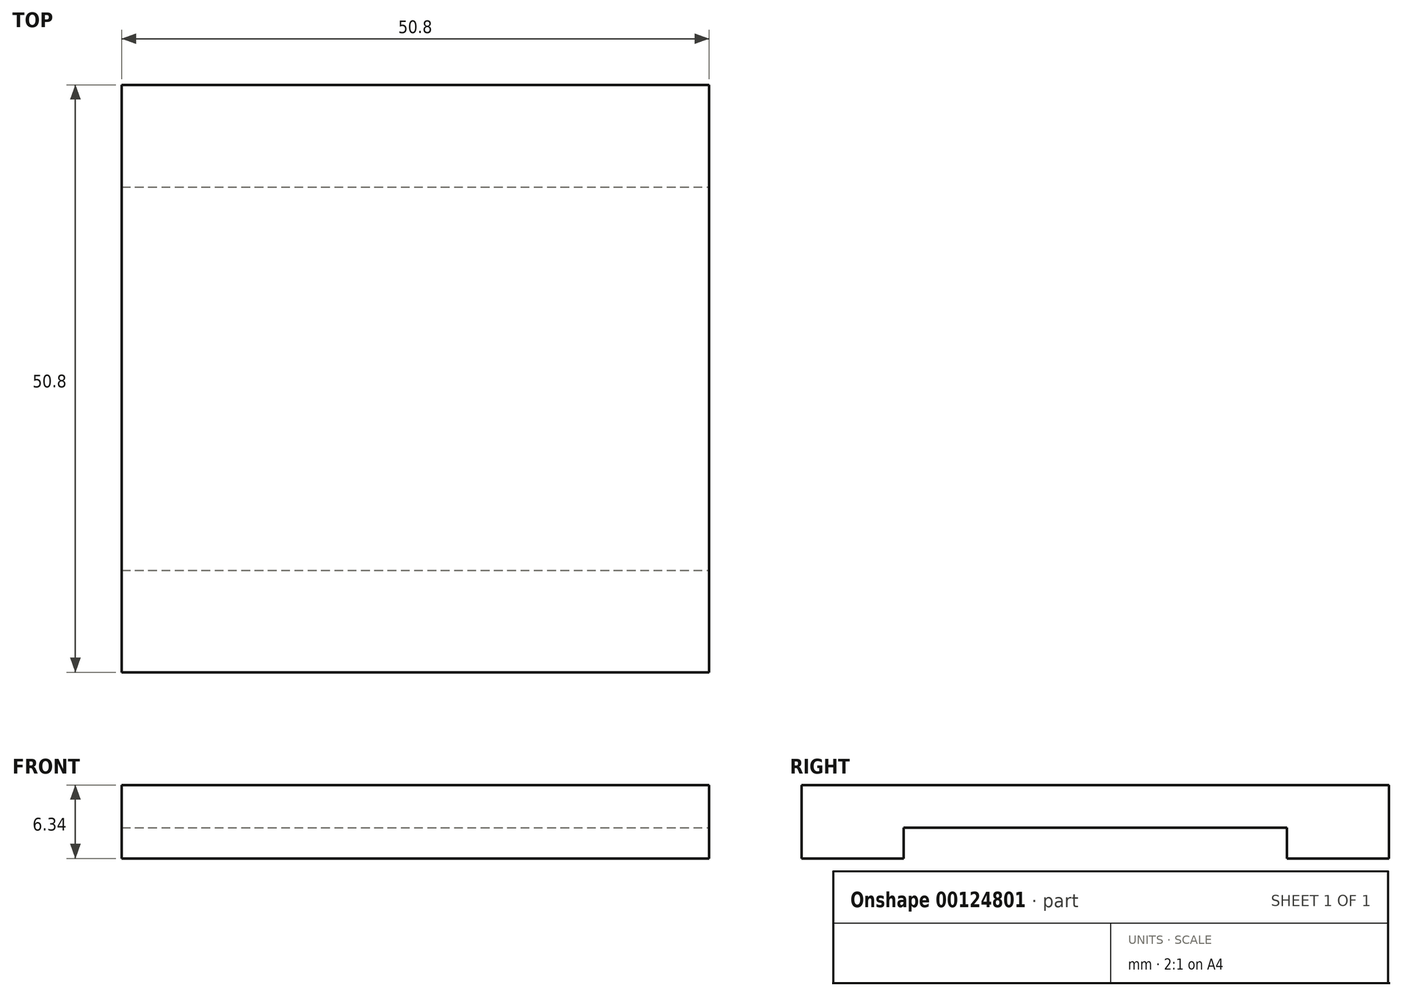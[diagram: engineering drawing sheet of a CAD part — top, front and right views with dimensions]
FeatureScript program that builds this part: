
annotation { "Feature Type Name" : "Feature", "Feature Type Description" : "" }
export const myFeature = defineFeature(function(context is Context, id is Id, definition is map)
    precondition{}
    {
        {
            var Q0;
            Q0=qCreatedBy(makeId("Top.planeOp"),FACE);
            var sketch = newSketch(context, id + "F0", { "sketchPlane" : qUnion([Q0])});
            skLineSegment(sketch, "E0.bottom", {"start": v(-26, 25.4) * mm, "end": v(24.8, 25.4) * mm});
            skLineSegment(sketch, "E0.top", {"start": v(-26, -25.4) * mm, "end": v(24.8, -25.4) * mm});
            skLineSegment(sketch, "E0.left", {"start": v(-26, 25.4) * mm, "end": v(-26, -25.4) * mm});
            skLineSegment(sketch, "E0.right", {"start": v(24.8, 25.4) * mm, "end": v(24.8, -25.4) * mm});
            skSolve(sketch);
        }
        {
            var Q0;
            Q0=makeQuery(id+"F0.imprint","IMPRINT",FACE,{"disambiguationData":[TD([[makeQuery(id+"F0.imprint","IMPRINT",EDGE,{"derivedFrom":sQuery(id+"F0.wireOp",EDGE,"E0.bottom")}),-1.0]])]});
            extrude(context, id + "F1", {"entities" : qUnion([Q0]), "endBound" : BoundingType.SYMMETRIC, "depth" : 6.35 * mm});
        }
        {
            var Q0;
            Q0=makeQuery(id+"F1.opExtrude","CAP_FACE",FACE,{"disambiguationData":[OSD([sQuery(id+"F0.wireOp",EDGE,"E0.bottom"),sQuery(id+"F0.wireOp",EDGE,"E0.top"),sQuery(id+"F0.wireOp",EDGE,"E0.left"),sQuery(id+"F0.wireOp",EDGE,"E0.right")])],"isStart":true});
            var sketch = newSketch(context, id + "F2", { "sketchPlane" : qUnion([Q0])});
            skLineSegment(sketch, "E1.bottom", {"start": v(-26, 16.57) * mm, "end": v(24.8, 16.57) * mm});
            skLineSegment(sketch, "E1.top", {"start": v(-26, -16.57) * mm, "end": v(24.8, -16.57) * mm});
            skLineSegment(sketch, "E1.left", {"start": v(-26, 16.57) * mm, "end": v(-26, -16.57) * mm});
            skLineSegment(sketch, "E1.right", {"start": v(24.8, 16.57) * mm, "end": v(24.8, -16.57) * mm});
            skSolve(sketch);
        }
        {
            var Q0;
            Q0=makeQuery(id+"F2.imprint","IMPRINT",FACE,{"disambiguationData":[TD([[makeQuery(id+"F2.imprint","IMPRINT",EDGE,{"derivedFrom":sQuery(id+"F2.wireOp",EDGE,"E1.bottom")}),-1.0]])]});
            extrude(context, id + "F3", {"entities" : qUnion([Q0]), "operationType" : NewBodyOperationType.REMOVE, "oppositeDirection" : true, "depth" : 2.67 * mm});
        }
    });
